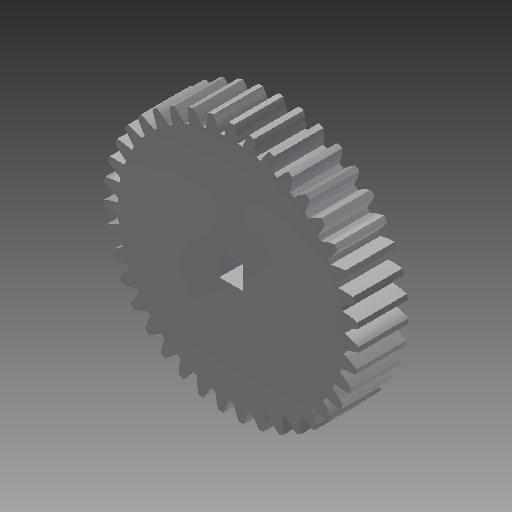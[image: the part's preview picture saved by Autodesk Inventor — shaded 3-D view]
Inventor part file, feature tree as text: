
AUTODESK INVENTOR PART (.ipt)
format: ipt  version: 2017 (Build 210142000, 142)  size: 310,784 bytes
history: native  units: mm (DEFAULTED — no unit token found)
features: plane x3, other x3, sketch x3, extrude x2
ambient origin geometry x8: Origin, YZ Plane, XZ Plane, XY Plane, X Axis, Y Axis, Z Axis, Center Point
bodies: Solid1 (feature_tree)
feature tree (11):
  extrude  "Extrusion1"  Depth=20.0mm TaperAngle=0.0deg
  plane  "Work Plane2"
  plane  "Work Plane8"
  plane  "Work Plane9"
  other  "Spur Gear"
  extrude  "Extrusion2"  Depth=10.0mm TaperAngle=0.0deg
  sketch  "Sketch1"  dims[d0=102.5mm d1=20.0mm d2=0.0mm]
  sketch  "Sketch2"  dims[d3=97.5mm d4=10.0mm d5=0.0mm]
  other  "Srf1"
  sketch  "Sketch3"  dims[d16=80.0mm d17=0.0mm d34=0.805537mm d39=0.0mm d41=0.0mm d43=80.0mm d46=80.0mm d47=0.0mm d48=0.0mm d49=9.525mm d50=10.0mm d51=0.0mm]
  other  "Pitch Diameter"
